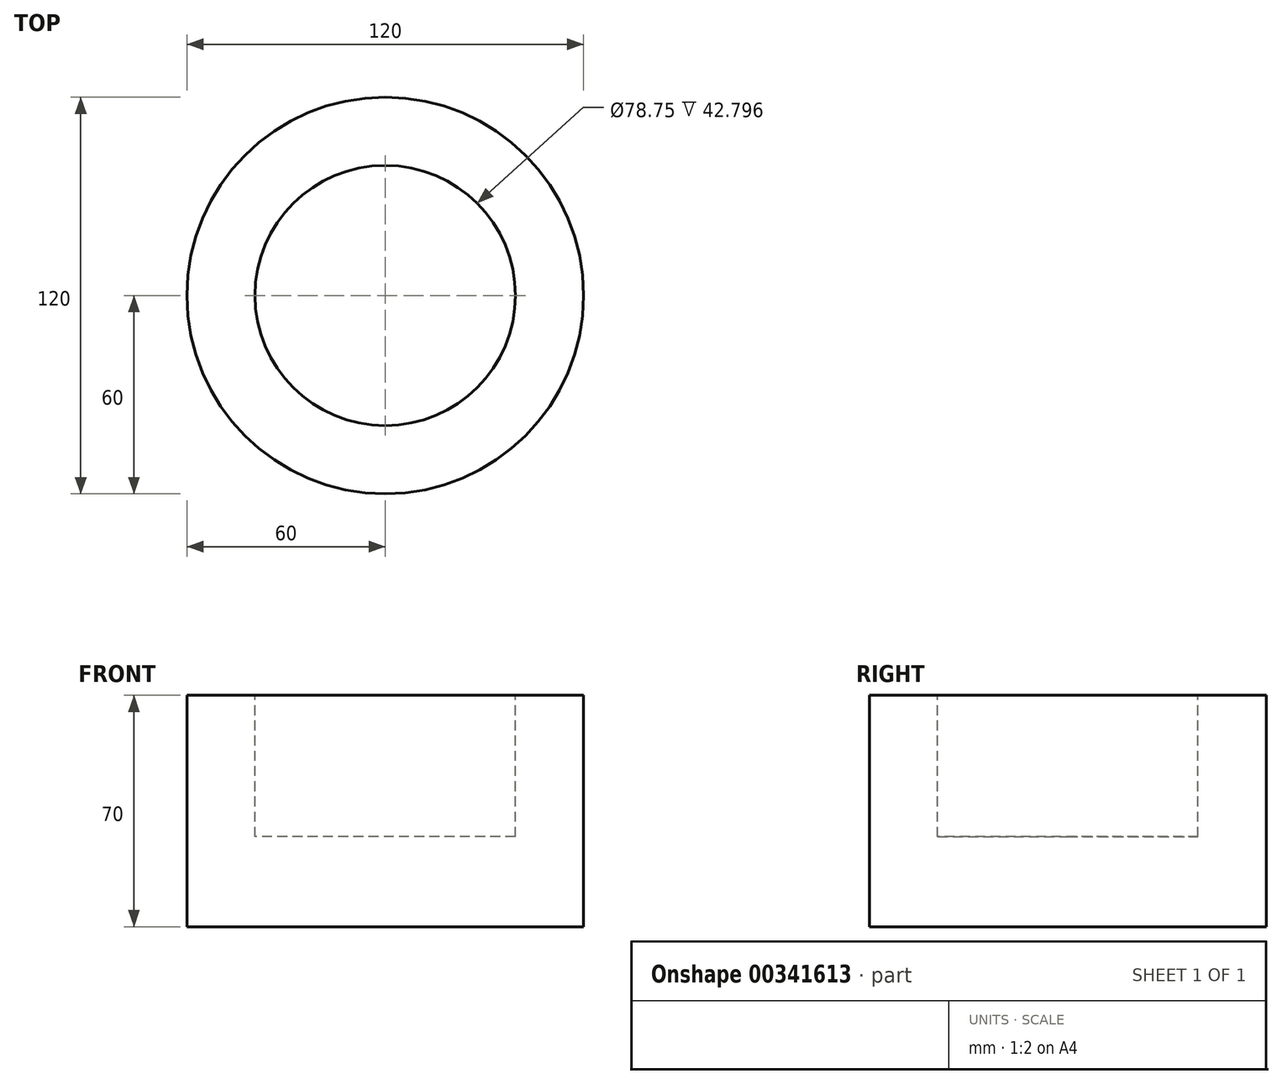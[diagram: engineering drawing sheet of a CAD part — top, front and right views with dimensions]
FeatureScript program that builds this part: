
annotation { "Feature Type Name" : "Feature", "Feature Type Description" : "" }
export const myFeature = defineFeature(function(context is Context, id is Id, definition is map)
    precondition{}
    {
        {
            var Q0;
            Q0=qCreatedBy(makeId("Right.planeOp"),FACE);
            var sketch = newSketch(context, id + "F0", { "sketchPlane" : qUnion([Q0])});
            skLineSegment(sketch, "E0", {"start": v(0, 80.04) * mm, "end": v(0, -73.37) * mm});
            skLineSegment(sketch, "E1.bottom", {"start": v(0, -73.37) * mm, "end": v(-60, -73.37) * mm});
            skLineSegment(sketch, "E1.left", {"start": v(0, -73.37) * mm, "end": v(0, -3.37) * mm});
            skLineSegment(sketch, "E1.right", {"start": v(-60, -73.37) * mm, "end": v(-60, -3.37) * mm});
            skLineSegment(sketch, "E2.right", {"start": v(0, 80.04) * mm, "end": v(0, -46.16) * mm});
            skPoint(sketch, "E2.left.start.orphan", {"position": v(-30, -3.37) * mm});
            skLineSegment(sketch, "E3", {"start": v(0, -46.16) * mm, "end": v(-39.37, -46.16) * mm});
            skLineSegment(sketch, "E4", {"start": v(-39.37, -46.16) * mm, "end": v(-39.37, -3.37) * mm});
            skLineSegment(sketch, "E5", {"start": v(-39.37, -3.37) * mm, "end": v(-60, -3.37) * mm});
            skSolve(sketch);
        }
        {
            var Q0;
            Q0=makeQuery(id+"F0.imprint","IMPRINT",FACE,{"disambiguationData":[TD([[makeQuery(id+"F0.imprint","IMPRINT",EDGE,{"derivedFrom":sQuery(id+"F0.wireOp",EDGE,"E1.bottom")}),-1.0]])]});
            var Q1;
            Q1=sQuery(id+"F0.wireOp",EDGE,"E2.right");
            revolve(context, id + "F1", {"entities" : qUnion([Q0]), "axis" : qUnion([Q1]), "revolveType" : RevolveType.FULL});
        }
    });
